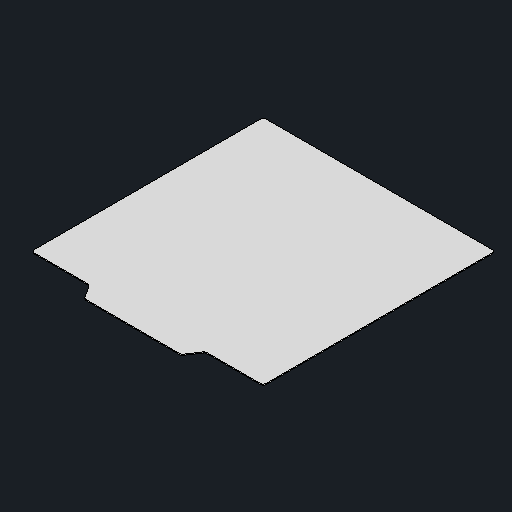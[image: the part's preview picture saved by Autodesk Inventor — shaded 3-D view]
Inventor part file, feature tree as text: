
AUTODESK INVENTOR PART (.ipt)
format: ipt  version: 2024.2 (Build 282272000, 272)  size: 80,896 bytes
history: native  units: mm
features: other x1, fillet x1
ambient origin geometry x8: Origin, YZ Plane, XZ Plane, XY Plane, X Axis, Y Axis, Z Axis, Center Point
bodies: Body1 (feature_tree)
feature tree (2):
  other  "솔리드1"
  fillet  "Fillet1"  [1 undecoded]
note: 1 required parameter value undecoded (feature->parameter linkage not recoverable at this tier; creation-order binding heuristic only, values carry confidence <= 0.55)
